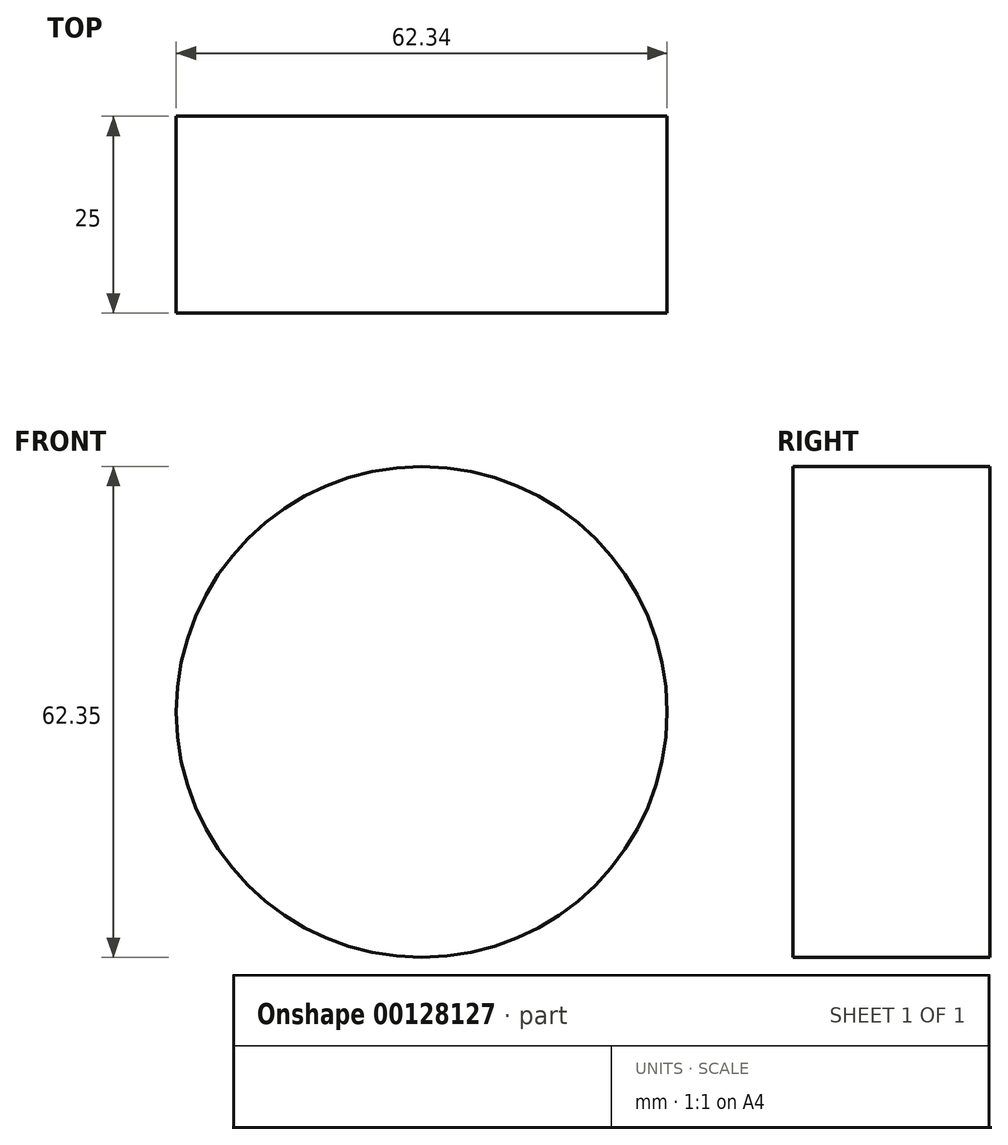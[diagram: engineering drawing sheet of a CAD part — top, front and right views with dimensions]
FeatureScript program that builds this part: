
annotation { "Feature Type Name" : "Feature", "Feature Type Description" : "" }
export const myFeature = defineFeature(function(context is Context, id is Id, definition is map)
    precondition{}
    {
        {
            var Q0;
            Q0=qCreatedBy(makeId("Front.planeOp"),FACE);
            var sketch = newSketch(context, id + "F0", { "sketchPlane" : qUnion([Q0])});
            skCircle(sketch, "E0", {"center": v(0, 0.5) * mm, "radius": 31.17 * mm});
            skSolve(sketch);
        }
        {
            var Q0;
            Q0 = qSketchRegion(id + "F0", true);
            extrude(context, id + "F1", {"entities" : qUnion([Q0]), "flatOperationType" : FlatOperationType.REMOVE, "offsetDistance" : 25 * mm, "depth" : 25 * mm, "domain" : OperationDomain.MODEL});
        }
    });
